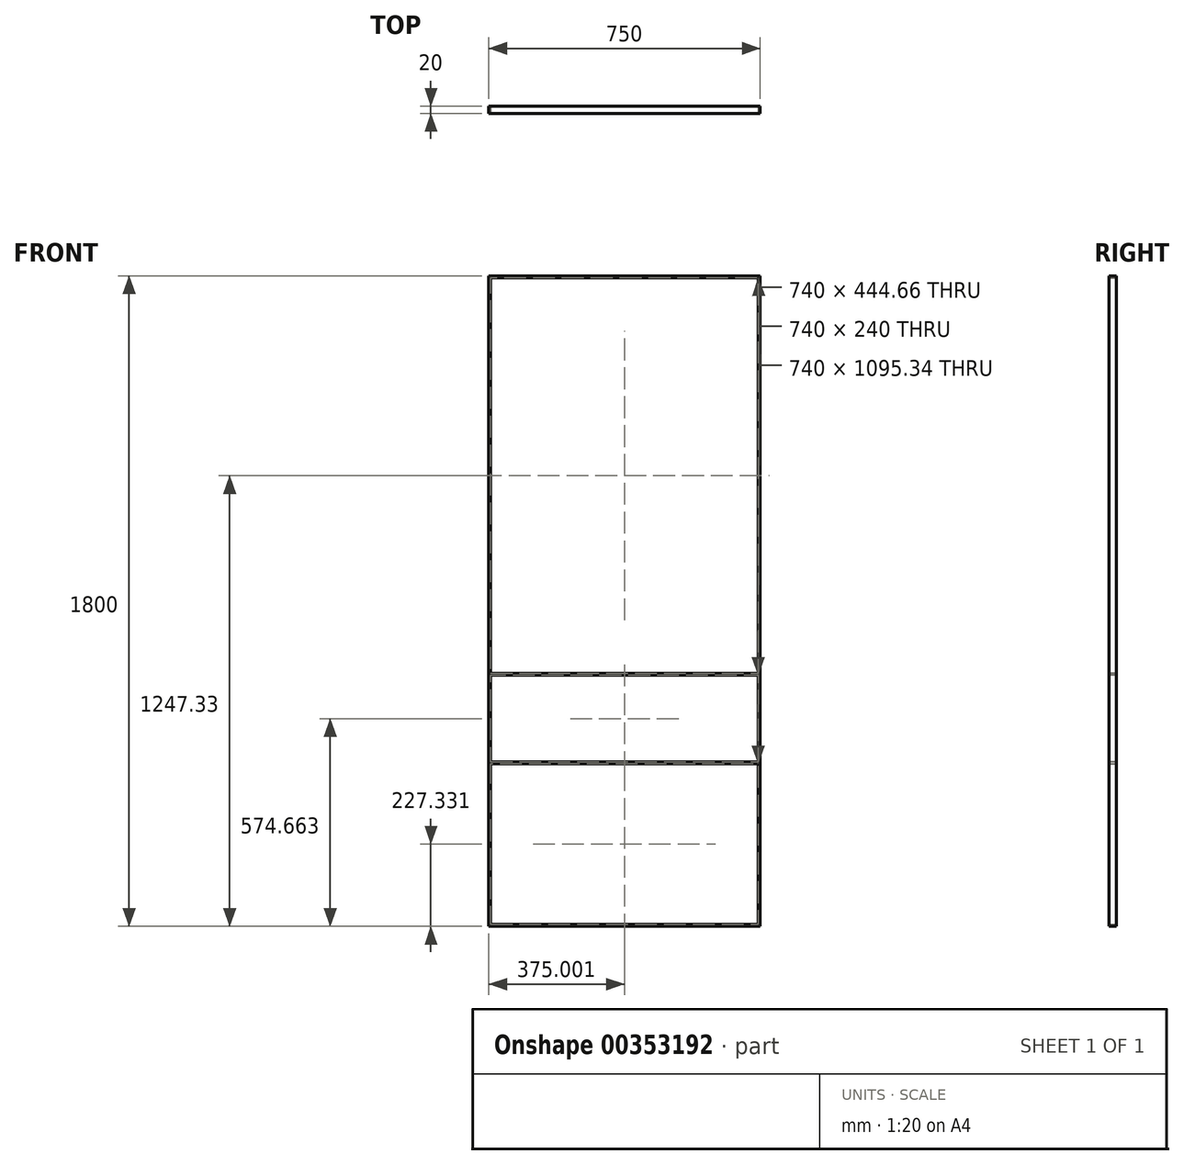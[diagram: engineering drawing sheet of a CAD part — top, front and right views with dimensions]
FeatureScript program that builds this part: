
annotation { "Feature Type Name" : "Feature", "Feature Type Description" : "" }
export const myFeature = defineFeature(function(context is Context, id is Id, definition is map)
    precondition{}
    {
        {
            var Q0;
            Q0=qCreatedBy(makeId("Front.planeOp"),FACE);
            var sketch = newSketch(context, id + "F0", { "sketchPlane" : qUnion([Q0])});
            skLineSegment(sketch, "E0.bottom", {"start": v(-77.64, 1491.84) * mm, "end": v(672.36, 1491.84) * mm});
            skLineSegment(sketch, "E0.top", {"start": v(-77.64, -308.16) * mm, "end": v(672.36, -308.16) * mm});
            skLineSegment(sketch, "E0.left", {"start": v(-77.64, 1491.84) * mm, "end": v(-77.64, -308.16) * mm});
            skLineSegment(sketch, "E0.right", {"start": v(672.36, 1491.84) * mm, "end": v(672.36, -308.16) * mm});
            skLineSegment(sketch, "E1.0", {"start": v(-72.64, 1486.84) * mm, "end": v(-72.64, -303.16) * mm});
            skLineSegment(sketch, "E1.1", {"start": v(-72.64, 1486.84) * mm, "end": v(667.36, 1486.84) * mm});
            skLineSegment(sketch, "E1.2", {"start": v(667.36, 1486.84) * mm, "end": v(667.36, -303.16) * mm});
            skLineSegment(sketch, "E1.3", {"start": v(-72.64, -303.16) * mm, "end": v(667.36, -303.16) * mm});
            skSolve(sketch);
        }
        {
            var Q0;
            Q0 = qSketchRegion(id + "F0", true);
            extrude(context, id + "F1", {"entities" : qUnion([Q0]), "depth" : 20 * mm});
        }
        {
            var Q0;
            Q0=qCreatedBy(makeId("Front.planeOp"),FACE);
            var sketch = newSketch(context, id + "F2", { "sketchPlane" : qUnion([Q0])});
            skLineSegment(sketch, "E2.bottom", {"start": v(-76.9, 391.5) * mm, "end": v(672.08, 391.5) * mm});
            skLineSegment(sketch, "E2.top", {"start": v(-76.9, 386.5) * mm, "end": v(672.08, 386.5) * mm});
            skLineSegment(sketch, "E2.left", {"start": v(-76.9, 391.5) * mm, "end": v(-76.9, 386.5) * mm});
            skLineSegment(sketch, "E2.right", {"start": v(672.08, 391.5) * mm, "end": v(672.08, 386.5) * mm});
            skLineSegment(sketch, "E3", {"start": v(-75.04, 146.5) * mm, "end": v(669.44, 146.5) * mm});
            skLineSegment(sketch, "E4", {"start": v(669.44, 146.5) * mm, "end": v(669.44, 141.5) * mm});
            skLineSegment(sketch, "E5", {"start": v(669.44, 141.5) * mm, "end": v(-75.04, 141.5) * mm});
            skLineSegment(sketch, "E6", {"start": v(-75.04, 146.5) * mm, "end": v(-75.04, 141.5) * mm});
            skPoint(sketch, "E7.end.orphan", {"position": v(297.6, 146.5) * mm});
            skPoint(sketch, "E7.start.orphan", {"position": v(297.6, 386.5) * mm});
            skSolve(sketch);
        }
        {
            var Q0;
            Q0 = qSketchRegion(id + "F2", true);
            extrude(context, id + "F3", {"entities" : qUnion([Q0]), "operationType" : NewBodyOperationType.ADD, "depth" : 20 * mm});
        }
    });
